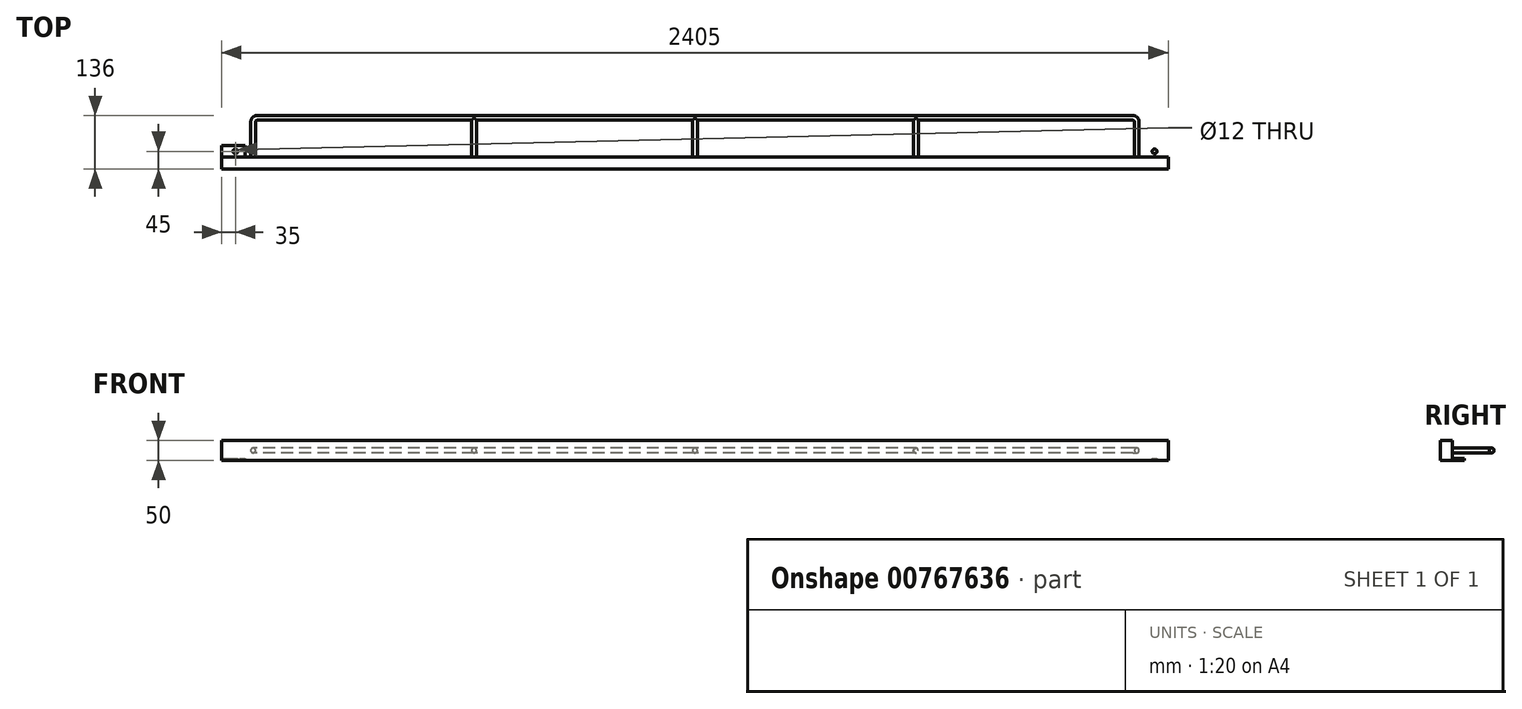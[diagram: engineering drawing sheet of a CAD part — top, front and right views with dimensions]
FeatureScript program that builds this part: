
annotation { "Feature Type Name" : "Feature", "Feature Type Description" : "" }
export const myFeature = defineFeature(function(context is Context, id is Id, definition is map)
    precondition{}
    {
        {
            var Q0;
            Q0=qCreatedBy(makeId("Front.planeOp"),FACE);
            var sketch = newSketch(context, id + "F0", { "sketchPlane" : qUnion([Q0])});
            skLineSegment(sketch, "E0.bottom", {"start": v(1202.5, -25) * mm, "end": v(-1202.5, -25) * mm});
            skLineSegment(sketch, "E0.top", {"start": v(1202.5, 25) * mm, "end": v(-1202.5, 25) * mm});
            skLineSegment(sketch, "E0.left", {"start": v(1202.5, -25) * mm, "end": v(1202.5, 25) * mm});
            skLineSegment(sketch, "E0.right", {"start": v(-1202.5, -25) * mm, "end": v(-1202.5, 25) * mm});
            skPoint(sketch, "E0.middle", {"position": v(0, 0) * mm});
            skSolve(sketch);
        }
        {
            var Q0;
            Q0=qSketchRegion(id+"F0",true);
            extrude(context, id + "F1", {"entities" : qUnion([Q0]), "depth" : 15 * mm, "offsetDistance" : 25 * mm, "hasSecondDirection" : true, "secondDirectionOppositeDirection" : true, "secondDirectionDepth" : 15 * mm});
        }
        {
            var Q0;
            Q0=makeQuery(id+"F1.opExtrude","SWEPT_FACE",FACE,{"disambiguationData":[OSD([sQuery(id+"F0.wireOp",EDGE,"E0.bottom")])]});
            var sketch = newSketch(context, id + "F2", { "sketchPlane" : qUnion([Q0])});
            skLineSegment(sketch, "E1.0", {"start": v(-1202.5, 15) * mm, "end": v(-1202.5, -15) * mm});
            skLineSegment(sketch, "E2.bottom", {"start": v(-1202.5, -15) * mm, "end": v(-1142.5, -15) * mm});
            skLineSegment(sketch, "E2.top", {"start": v(-1202.5, 45) * mm, "end": v(-1142.5, 45) * mm});
            skLineSegment(sketch, "E2.left", {"start": v(-1202.5, -15) * mm, "end": v(-1202.5, 45) * mm});
            skLineSegment(sketch, "E2.right", {"start": v(-1142.5, -15) * mm, "end": v(-1142.5, 45) * mm});
            skLineSegment(sketch, "E3", {"start": v(-1773.05, 0) * mm, "end": v(-1202.5, 0) * mm});
            skLineSegment(sketch, "E4.MirrorCS", {"start": v(-1202.5, -15) * mm, "end": v(-1202.5, 15) * mm});
            skLineSegment(sketch, "E5.MirrorCS", {"start": v(-1202.5, 15) * mm, "end": v(-1202.5, -45) * mm});
            skLineSegment(sketch, "E6.MirrorCS", {"start": v(-1202.5, -45) * mm, "end": v(-1142.5, -45) * mm});
            skLineSegment(sketch, "E7.MirrorCS", {"start": v(-1142.5, 15) * mm, "end": v(-1142.5, -45) * mm});
            skSolve(sketch);
        }
        {
            var Q0;
            {var subQ0=sQuery(id+"F2.wireOp",EDGE,"E2.bottom");Q0=makeQuery(id+"F2.imprint","IMPRINT",FACE,{"disambiguationData":[TD([[makeQuery(id+"F2.imprint","IMPRINT",EDGE,{"derivedFrom":subQ0}),1.0]])]});}
            var Q1;
            {var subQ1=sQuery(id+"F2.wireOp",EDGE,"E2.bottom");Q1=makeQuery(id+"F2.imprint","IMPRINT",FACE,{"disambiguationData":[TD([[makeQuery(id+"F2.imprint","IMPRINT",EDGE,{"derivedFrom":subQ1}),-1.0]])]});}
            extrude(context, id + "F3", {"entities" : qUnion([Q0, Q1]), "operationType" : NewBodyOperationType.ADD, "depth" : 5 * mm, "offsetDistance" : 25 * mm});
        }
        {
            var Q0;
            Q0=makeQuery(id+"F1.opExtrude","SWEPT_FACE",FACE,{"disambiguationData":[OSD([sQuery(id+"F0.wireOp",EDGE,"E0.bottom")])]});
            var sketch = newSketch(context, id + "F4", { "sketchPlane" : qUnion([Q0])});
            skLineSegment(sketch, "E8.0", {"start": v(1202.5, 15) * mm, "end": v(1202.5, -15) * mm});
            skLineSegment(sketch, "E9.bottom", {"start": v(1202.5, -15) * mm, "end": v(1142.5, -15) * mm});
            skLineSegment(sketch, "E9.top", {"start": v(1202.5, 45) * mm, "end": v(1142.5, 45) * mm});
            skLineSegment(sketch, "E9.left", {"start": v(1202.5, -15) * mm, "end": v(1202.5, 45) * mm});
            skLineSegment(sketch, "E9.right", {"start": v(1142.5, -15) * mm, "end": v(1142.5, 45) * mm});
            skLineSegment(sketch, "E10", {"start": v(1727.5, 0) * mm, "end": v(1202.5, 0) * mm});
            skLineSegment(sketch, "E11.MirrorCS", {"start": v(1202.5, 15) * mm, "end": v(1202.5, -45) * mm});
            skLineSegment(sketch, "E12.MirrorCS", {"start": v(1202.5, -45) * mm, "end": v(1142.5, -45) * mm});
            skLineSegment(sketch, "E13.MirrorCS", {"start": v(1142.5, 15) * mm, "end": v(1142.5, -45) * mm});
            skSolve(sketch);
        }
        {
            var Q0;
            {var subQ0=sQuery(id+"F4.wireOp",EDGE,"E9.bottom");Q0=makeQuery(id+"F4.imprint","IMPRINT",FACE,{"disambiguationData":[TD([[makeQuery(id+"F4.imprint","IMPRINT",EDGE,{"derivedFrom":subQ0}),1.0]])]});}
            var Q1;
            {var subQ1=sQuery(id+"F4.wireOp",EDGE,"E9.bottom");Q1=makeQuery(id+"F4.imprint","IMPRINT",FACE,{"disambiguationData":[TD([[makeQuery(id+"F4.imprint","IMPRINT",EDGE,{"derivedFrom":subQ1}),-1.0]])]});}
            var Q2;
            {var subQ0=sQuery(id+"F4.wireOp",EDGE,"E11.MirrorCS");var subQ1=sQuery(id+"F4.wireOp",EDGE,"E10");var subQ2=makeQuery(id+"F4.imprint","INTERSECT",VERTEX,{"derivedFrom":[subQ1,subQ0]});Q2=makeQuery(id+"F4.imprint","IMPRINT",FACE,{"disambiguationData":[TD([[makeQuery(id+"F4.imprint","IMPRINT",EDGE,{"disambiguationData":[TD([[subQ2,-1.0]])],"derivedFrom":subQ1}),-1.0]])]});}
            extrude(context, id + "F5", {"entities" : qUnion([Q0, Q1, Q2]), "operationType" : NewBodyOperationType.ADD, "depth" : 5 * mm, "offsetDistance" : 25 * mm});
        }
        {
            var Q0;
            Q0=makeQuery(id+"F5.opExtrude","CAP_FACE",FACE,{"disambiguationData":[OSD([sQuery(id+"F0.wireOp",EDGE,"E0.bottom"),sQuery(id+"F4.wireOp",EDGE,"E11.MirrorCS"),sQuery(id+"F4.wireOp",EDGE,"E12.MirrorCS"),sQuery(id+"F4.wireOp",EDGE,"E13.MirrorCS")])],"isStart":false});
            var sketch = newSketch(context, id + "F6", { "sketchPlane" : qUnion([Q0])});
            skCircle(sketch, "E14.0", {"center": v(1762.5, 0) * mm, "radius": 6 * mm});
            skCircle(sketch, "E15.0", {"center": v(1722.5, 0) * mm, "radius": 6 * mm});
            skLineSegment(sketch, "E16", {"start": v(1202.5, 15) * mm, "end": v(1202.5, -45) * mm});
            skCircle(sketch, "E17.MirrorC", {"center": v(1167.5, -30) * mm, "radius": 6 * mm});
            skLineSegment(sketch, "E18.0", {"start": v(1202.5, -15) * mm, "end": v(1202.5, -45) * mm});
            skLineSegment(sketch, "E19", {"start": v(1167.5, -30) * mm, "end": v(1202.5, -30) * mm});
            skSolve(sketch);
        }
        {
            var Q0;
            Q0=makeQuery(id+"F6.imprint","IMPRINT",FACE,{"disambiguationData":[TD([[makeQuery(id+"F6.imprint","IMPRINT",EDGE,{"derivedFrom":sQuery(id+"F6.wireOp",EDGE,"E17.MirrorC")}),-1.0]])]});
            var Q1;
            Q1=makeQuery(id+"F6.imprint","IMPRINT",FACE,{"disambiguationData":[TD([[makeQuery(id+"F6.imprint","IMPRINT",EDGE,{"derivedFrom":sQuery(id+"F6.wireOp",EDGE,"f1c2a5ba-6244-45c4-a5ad-aa170d6a38100.MirrorC")}),-1.0]])]});
            var Q2;
            Q2=makeQuery(id+"F5.opExtrude","CAP_FACE",FACE,{"disambiguationData":[OSD([sQuery(id+"F0.wireOp",EDGE,"E0.bottom"),sQuery(id+"F4.wireOp",EDGE,"E11.MirrorCS"),sQuery(id+"F4.wireOp",EDGE,"E12.MirrorCS"),sQuery(id+"F4.wireOp",EDGE,"E13.MirrorCS")])],"isStart":true});
            extrude(context, id + "F7", {"entities" : qUnion([Q0, Q1]), "operationType" : NewBodyOperationType.REMOVE, "endBound" : BoundingType.UP_TO_SURFACE, "oppositeDirection" : true, "depth" : 25 * mm, "endBoundEntityFace" : qUnion([Q2]), "offsetDistance" : 25 * mm});
        }
        {
            var Q0;
            Q0=makeQuery(id+"F3.opExtrude","CAP_FACE",FACE,{"disambiguationData":[OSD([sQuery(id+"F0.wireOp",EDGE,"E0.bottom"),sQuery(id+"F2.wireOp",EDGE,"E5.MirrorCS"),sQuery(id+"F2.wireOp",EDGE,"E6.MirrorCS"),sQuery(id+"F2.wireOp",EDGE,"E7.MirrorCS")])],"isStart":false});
            var sketch = newSketch(context, id + "F8", { "sketchPlane" : qUnion([Q0])});
            skLineSegment(sketch, "E20.bottom", {"start": v(-1202.5, 15) * mm, "end": v(-1177.5, 15) * mm, "construction": true});
            skLineSegment(sketch, "E20.top", {"start": v(-1202.5, 0) * mm, "end": v(-1177.5, 0) * mm});
            skLineSegment(sketch, "E20.left", {"start": v(-1202.5, 15) * mm, "end": v(-1202.5, 0) * mm});
            skLineSegment(sketch, "E20.right", {"start": v(-1177.5, 15) * mm, "end": v(-1177.5, 0) * mm});
            skLineSegment(sketch, "E21", {"start": v(-1177.5, 0) * mm, "end": v(-1137.5, 0) * mm});
            skLineSegment(sketch, "E22", {"start": v(-1142.5, 15) * mm, "end": v(-1142.5, -45) * mm});
            skLineSegment(sketch, "E23", {"start": v(-1142.5, -15) * mm, "end": v(-1161.34, -15) * mm});
            skCircle(sketch, "E24.MirrorC", {"center": v(-1167.5, -30) * mm, "radius": 6 * mm});
            skLineSegment(sketch, "E25", {"start": v(-1167.5, -30) * mm, "end": v(-1202.5, -30) * mm});
            skSolve(sketch);
        }
        {
            var Q0;
            Q0=qSketchRegion(id+"F8",true);
            extrude(context, id + "F9", {"entities" : qUnion([Q0]), "operationType" : NewBodyOperationType.REMOVE, "endBound" : BoundingType.UP_TO_NEXT, "oppositeDirection" : true, "depth" : 25 * mm, "offsetDistance" : 25 * mm});
        }
        {
            var Q0;
            Q0=makeQuery(id+"F5.opExtrude","CAP_FACE",FACE,{"disambiguationData":[OSD([sQuery(id+"F0.wireOp",EDGE,"E0.bottom"),sQuery(id+"F4.wireOp",EDGE,"E11.MirrorCS"),sQuery(id+"F4.wireOp",EDGE,"E12.MirrorCS"),sQuery(id+"F4.wireOp",EDGE,"E13.MirrorCS")])],"isStart":true});
            var Q1;
            Q1=makeQuery(id+"F3.opExtrude","CAP_FACE",FACE,{"disambiguationData":[OSD([sQuery(id+"F0.wireOp",EDGE,"E0.bottom"),sQuery(id+"F2.wireOp",EDGE,"E5.MirrorCS"),sQuery(id+"F2.wireOp",EDGE,"E6.MirrorCS"),sQuery(id+"F2.wireOp",EDGE,"E7.MirrorCS")])],"isStart":true});
            extrude(context, id + "F10", {"entities" : qUnion([Q0, Q1]), "operationType" : NewBodyOperationType.ADD, "depth" : 5 * mm, "offsetDistance" : 25 * mm});
        }
        {
            var Q0;
            Q0=makeQuery(id+"F3.opExtrude","CAP_FACE",FACE,{"disambiguationData":[OSD([sQuery(id+"F0.wireOp",EDGE,"E0.bottom"),sQuery(id+"F2.wireOp",EDGE,"E5.MirrorCS"),sQuery(id+"F2.wireOp",EDGE,"E6.MirrorCS"),sQuery(id+"F2.wireOp",EDGE,"E7.MirrorCS")])],"isStart":false});
            var Q1;
            Q1=makeQuery(id+"F5.opExtrude","CAP_FACE",FACE,{"disambiguationData":[OSD([sQuery(id+"F0.wireOp",EDGE,"E0.bottom"),sQuery(id+"F4.wireOp",EDGE,"E11.MirrorCS"),sQuery(id+"F4.wireOp",EDGE,"E12.MirrorCS"),sQuery(id+"F4.wireOp",EDGE,"E13.MirrorCS")])],"isStart":false});
            extrude(context, id + "F11", {"entities" : qUnion([Q0, Q1]), "operationType" : NewBodyOperationType.REMOVE, "oppositeDirection" : true, "depth" : 5 * mm, "offsetDistance" : 25 * mm});
        }
        {
            var Q0;
            Q0=makeQuery(id+"F1.opExtrude","CAP_FACE",FACE,{"disambiguationData":[OSD([sQuery(id+"F0.wireOp",EDGE,"E0.bottom"),sQuery(id+"F0.wireOp",EDGE,"E0.top"),sQuery(id+"F0.wireOp",EDGE,"E0.left"),sQuery(id+"F0.wireOp",EDGE,"E0.right")])],"isStart":true});
            var sketch = newSketch(context, id + "F12", { "sketchPlane" : qUnion([Q0])});
            skLineSegment(sketch, "E26", {"start": v(-1142.5, -25) * mm, "end": v(-1142.5, 25) * mm, "construction": true});
            skLineSegment(sketch, "E27", {"start": v(-1142.5, 25) * mm, "end": v(-1122.5, 25) * mm});
            skLineSegment(sketch, "E28", {"start": v(-1122.5, 25) * mm, "end": v(-1122.5, 0) * mm});
            skLineSegment(sketch, "E29", {"start": v(1142.5, -25) * mm, "end": v(1142.5, 0) * mm});
            skPoint(sketch, "E30.orphan", {"position": v(-1142.5, 0) * mm});
            skCircle(sketch, "E31", {"center": v(1122.5, 0) * mm, "radius": 6 * mm});
            skCircle(sketch, "E32", {"center": v(0, 0) * mm, "radius": 6 * mm});
            skCircle(sketch, "E33", {"center": v(-1122.5, 0) * mm, "radius": 6 * mm});
            skLineSegment(sketch, "E34", {"start": v(-1122.5, 0) * mm, "end": v(0, 0) * mm});
            skLineSegment(sketch, "E35", {"start": v(0, 0) * mm, "end": v(1122.5, 0) * mm});
            skCircle(sketch, "E36", {"center": v(561.25, 0) * mm, "radius": 6 * mm});
            skCircle(sketch, "E37", {"center": v(-561.25, 0) * mm, "radius": 6 * mm});
            skSolve(sketch);
        }
        {
            var Q0;
            Q0=qCreatedBy(makeId("Top.planeOp"),FACE);
            var sketch = newSketch(context, id + "F13", { "sketchPlane" : qUnion([Q0])});
            skLineSegment(sketch, "E38", {"start": v(1122.5, 105) * mm, "end": v(1122.5, 15) * mm});
            skLineSegment(sketch, "E39", {"start": v(561.25, 115) * mm, "end": v(561.25, 15) * mm});
            skLineSegment(sketch, "E40", {"start": v(0, 115) * mm, "end": v(0, 15) * mm});
            skLineSegment(sketch, "E41", {"start": v(-561.25, 115) * mm, "end": v(-561.25, 15) * mm});
            skLineSegment(sketch, "E42", {"start": v(-1122.5, 105) * mm, "end": v(-1122.5, 15) * mm});
            skLineSegment(sketch, "E43", {"start": v(-1122.5, 105) * mm, "end": v(-1112.5, 105) * mm, "construction": true});
            skArc(sketch, "E44", {"start": v(-1112.5, 115) * mm, "mid": v(-1119.57, 112.07) * mm, "end": v(-1122.5, 105) * mm});
            skLineSegment(sketch, "E45", {"start": v(-1112.5, 105) * mm, "end": v(-1112.5, 115) * mm});
            skLineSegment(sketch, "E46", {"start": v(-1112.5, 115) * mm, "end": v(1112.5, 115) * mm});
            skLineSegment(sketch, "E47", {"start": v(1122.5, 105) * mm, "end": v(1112.5, 105) * mm});
            skLineSegment(sketch, "E48", {"start": v(1112.5, 105) * mm, "end": v(1112.5, 115) * mm, "construction": true});
            skArc(sketch, "E49", {"start": v(1122.5, 105) * mm, "mid": v(1119.57, 112.07) * mm, "end": v(1112.5, 115) * mm});
            skSolve(sketch);
        }
        {
            var Q0;
            {var subQ0=sQuery(id+"F12.wireOp",EDGE,"E34");var subQ1=sQuery(id+"F12.wireOp",EDGE,"E28");var subQ2=makeQuery(id+"F12.imprint","INTERSECT",VERTEX,{"derivedFrom":[subQ1,subQ0]});Q0=makeQuery(id+"F12.imprint","IMPRINT",FACE,{"disambiguationData":[TD([[makeQuery(id+"F12.imprint","IMPRINT",EDGE,{"disambiguationData":[TD([[subQ2,1.0]])],"derivedFrom":subQ1}),-1.0]])]});}
            var Q1;
            {var subQ0=sQuery(id+"F12.wireOp",EDGE,"E34");var subQ1=sQuery(id+"F12.wireOp",EDGE,"E28");var subQ2=makeQuery(id+"F12.imprint","INTERSECT",VERTEX,{"derivedFrom":[subQ1,subQ0]});Q1=makeQuery(id+"F12.imprint","IMPRINT",FACE,{"disambiguationData":[TD([[makeQuery(id+"F12.imprint","IMPRINT",EDGE,{"disambiguationData":[TD([[subQ2,1.0]])],"derivedFrom":subQ1}),1.0]])]});}
            var Q2;
            Q2=sQuery(id+"F13.wireOp",EDGE,"E38");
            var Q3;
            Q3=sQuery(id+"F13.wireOp",EDGE,"E49");
            var Q4;
            Q4=sQuery(id+"F13.wireOp",EDGE,"E46");
            var Q5;
            Q5=sQuery(id+"F13.wireOp",EDGE,"E44");
            var Q6;
            Q6=sQuery(id+"F13.wireOp",EDGE,"E42");
            sweep(context, id + "F14", {"operationType" : NewBodyOperationType.ADD, "profiles" : qUnion([Q0, Q1]), "path" : qUnion([Q2, Q3, Q4, Q5, Q6])});
        }
        {
            var Q0;
            {var subQ0=sQuery(id+"F12.wireOp",EDGE,"E36");var subQ1=sQuery(id+"F12.wireOp",EDGE,"E35");var subQ2=makeQuery(id+"F12.imprint","INTERSECT",VERTEX,{"disambiguationData":[OD(0.0)],"derivedFrom":[subQ1,subQ0]});Q0=makeQuery(id+"F12.imprint","IMPRINT",FACE,{"disambiguationData":[TD([[makeQuery(id+"F12.imprint","IMPRINT",EDGE,{"disambiguationData":[TD([[subQ2,1.0]])],"derivedFrom":subQ1}),1.0]])]});}
            var Q1;
            {var subQ0=sQuery(id+"F12.wireOp",EDGE,"E36");var subQ1=sQuery(id+"F12.wireOp",EDGE,"E35");var subQ2=makeQuery(id+"F12.imprint","INTERSECT",VERTEX,{"disambiguationData":[OD(0.0)],"derivedFrom":[subQ1,subQ0]});Q1=makeQuery(id+"F12.imprint","IMPRINT",FACE,{"disambiguationData":[TD([[makeQuery(id+"F12.imprint","IMPRINT",EDGE,{"disambiguationData":[TD([[subQ2,1.0]])],"derivedFrom":subQ1}),-1.0]])]});}
            var Q2;
            Q2=sQuery(id+"F13.wireOp",EDGE,"E41");
            sweep(context, id + "F15", {"operationType" : NewBodyOperationType.ADD, "profiles" : qUnion([Q0, Q1]), "path" : qUnion([Q2])});
        }
        {
            var Q0;
            {var subQ0=sQuery(id+"F12.wireOp",EDGE,"E34");var subQ1=sQuery(id+"F12.wireOp",EDGE,"E32");var subQ2=makeQuery(id+"F12.imprint","INTERSECT",VERTEX,{"derivedFrom":[subQ1,subQ0]});Q0=makeQuery(id+"F12.imprint","IMPRINT",FACE,{"disambiguationData":[TD([[makeQuery(id+"F12.imprint","IMPRINT",EDGE,{"disambiguationData":[TD([[subQ2,1.0]])],"derivedFrom":subQ1}),1.0]])]});}
            var Q1;
            {var subQ0=sQuery(id+"F12.wireOp",EDGE,"E34");var subQ1=sQuery(id+"F12.wireOp",EDGE,"E32");var subQ2=makeQuery(id+"F12.imprint","INTERSECT",VERTEX,{"derivedFrom":[subQ1,subQ0]});Q1=makeQuery(id+"F12.imprint","IMPRINT",FACE,{"disambiguationData":[TD([[makeQuery(id+"F12.imprint","IMPRINT",EDGE,{"disambiguationData":[TD([[subQ2,-1.0]])],"derivedFrom":subQ1}),1.0]])]});}
            var Q2;
            Q2=sQuery(id+"F13.wireOp",EDGE,"E40");
            sweep(context, id + "F16", {"operationType" : NewBodyOperationType.ADD, "profiles" : qUnion([Q0, Q1]), "path" : qUnion([Q2])});
        }
        {
            var Q0;
            {var subQ0=sQuery(id+"F12.wireOp",EDGE,"E37");var subQ1=sQuery(id+"F12.wireOp",EDGE,"E34");var subQ2=makeQuery(id+"F12.imprint","INTERSECT",VERTEX,{"disambiguationData":[OD(0.0)],"derivedFrom":[subQ1,subQ0]});Q0=makeQuery(id+"F12.imprint","IMPRINT",FACE,{"disambiguationData":[TD([[makeQuery(id+"F12.imprint","IMPRINT",EDGE,{"disambiguationData":[TD([[subQ2,1.0]])],"derivedFrom":subQ1}),1.0]])]});}
            var Q1;
            {var subQ0=sQuery(id+"F12.wireOp",EDGE,"E37");var subQ1=sQuery(id+"F12.wireOp",EDGE,"E34");var subQ2=makeQuery(id+"F12.imprint","INTERSECT",VERTEX,{"disambiguationData":[OD(0.0)],"derivedFrom":[subQ1,subQ0]});Q1=makeQuery(id+"F12.imprint","IMPRINT",FACE,{"disambiguationData":[TD([[makeQuery(id+"F12.imprint","IMPRINT",EDGE,{"disambiguationData":[TD([[subQ2,1.0]])],"derivedFrom":subQ1}),-1.0]])]});}
            var Q2;
            Q2=sQuery(id+"F13.wireOp",EDGE,"E39");
            sweep(context, id + "F17", {"operationType" : NewBodyOperationType.ADD, "profiles" : qUnion([Q0, Q1]), "path" : qUnion([Q2])});
        }
    });
